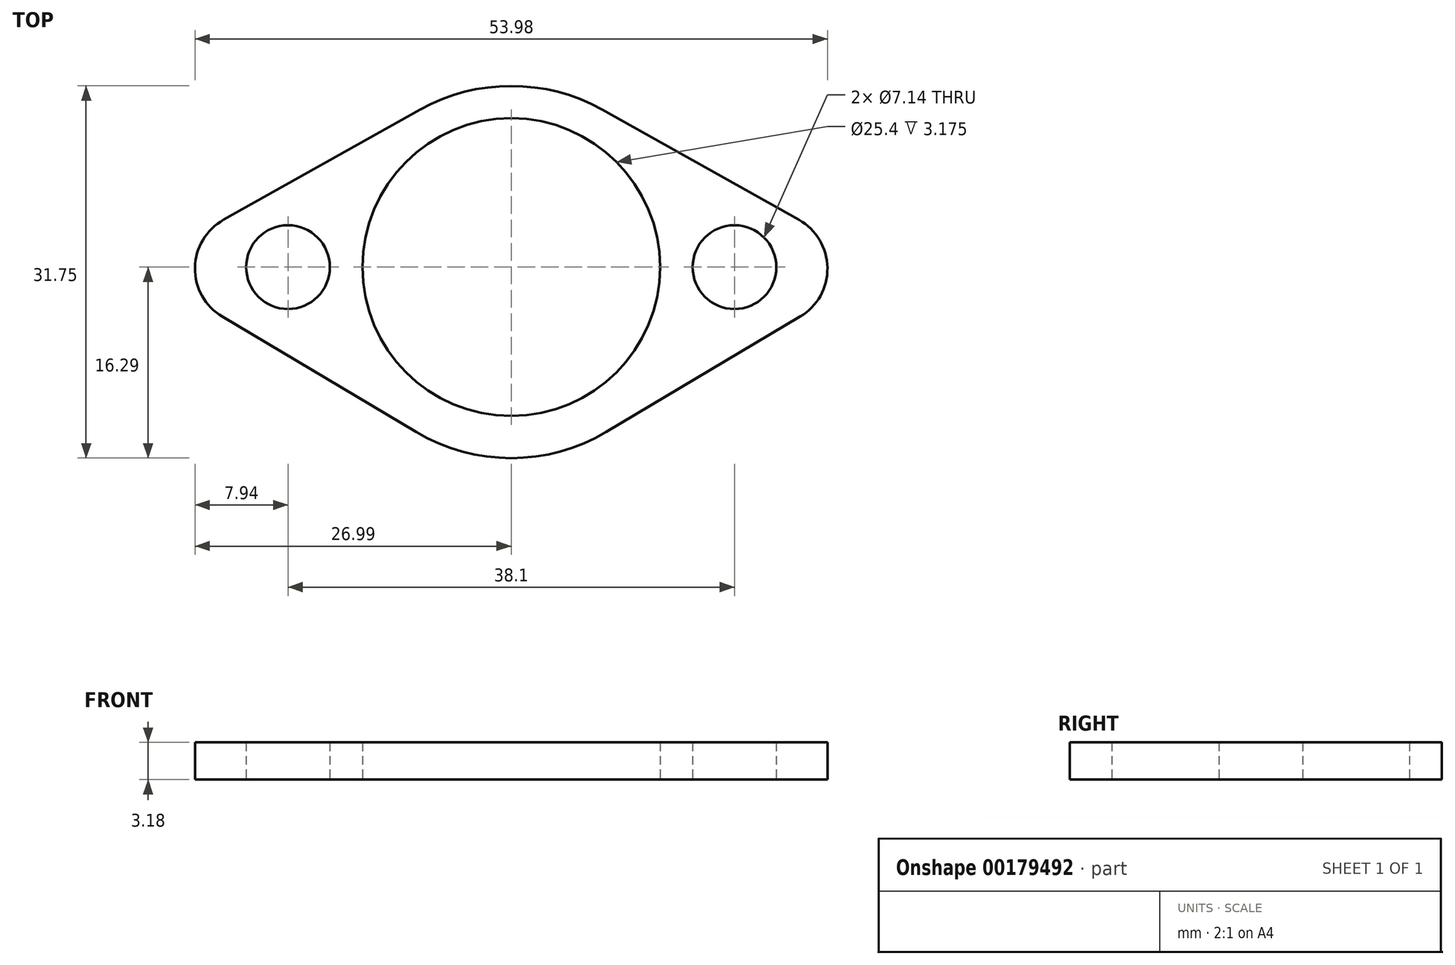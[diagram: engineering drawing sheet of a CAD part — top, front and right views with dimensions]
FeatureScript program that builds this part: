
annotation { "Feature Type Name" : "Feature", "Feature Type Description" : "" }
export const myFeature = defineFeature(function(context is Context, id is Id, definition is map)
    precondition{}
    {
        {
            var Q0;
            Q0=qCreatedBy(makeId("Top.planeOp"),FACE);
            var sketch = newSketch(context, id + "F0", { "sketchPlane" : qUnion([Q0])});
            skCircle(sketch, "E0", {"center": v(0, 0) * mm, "radius": 12.7 * mm});
            skCircle(sketch, "E1", {"center": v(-19.05, 0) * mm, "radius": 3.57 * mm});
            skCircle(sketch, "E2", {"center": v(19.05, 0) * mm, "radius": 3.57 * mm});
            skLineSegment(sketch, "E3", {"start": v(-24.55, 4.03) * mm, "end": v(-7.75, 13.43) * mm});
            skLineSegment(sketch, "E4", {"start": v(7.75, 13.43) * mm, "end": v(24.55, 4.03) * mm});
            skLineSegment(sketch, "E5", {"start": v(24.66, -4.22) * mm, "end": v(8.12, -14.06) * mm});
            skLineSegment(sketch, "E6", {"start": v(-8.12, -14.06) * mm, "end": v(-24.66, -4.22) * mm});
            skLineSegment(sketch, "E7", {"start": v(-19.05, 0) * mm, "end": v(19.05, 0) * mm});
            skPoint(sketch, "E8.visualSharp", {"position": v(0, 17.77) * mm});
            skArc(sketch, "E8.filletArc", {"start": v(7.75, 13.43) * mm, "mid": v(0, 15.46) * mm, "end": v(-7.75, 13.43) * mm});
            skPoint(sketch, "E9.visualSharp", {"position": v(0, -18.9) * mm});
            skArc(sketch, "E9.filletArc", {"start": v(-8.12, -14.06) * mm, "mid": v(0, -16.3) * mm, "end": v(8.12, -14.06) * mm});
            skPoint(sketch, "E10.visualSharp", {"position": v(-31.75, 0) * mm});
            skArc(sketch, "E10.filletArc", {"start": v(-24.55, 4.03) * mm, "mid": v(-26.99, -0.06) * mm, "end": v(-24.66, -4.22) * mm});
            skPoint(sketch, "E11.visualSharp", {"position": v(31.75, 0) * mm});
            skArc(sketch, "E11.filletArc", {"start": v(24.66, -4.22) * mm, "mid": v(26.99, -0.06) * mm, "end": v(24.55, 4.03) * mm});
            skSolve(sketch);
        }
        {
            var Q0;
            Q0=makeQuery(id+"F0.imprint","IMPRINT",FACE,{"disambiguationData":[TD([[makeQuery(id+"F0.imprint","IMPRINT",EDGE,{"derivedFrom":sQuery(id+"F0.wireOp",EDGE,"E1")}),-1.0]])]});
            extrude(context, id + "F1", {"entities" : qUnion([Q0]), "depth" : 3.17 * mm});
        }
    });
